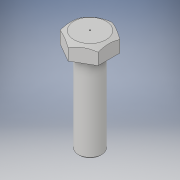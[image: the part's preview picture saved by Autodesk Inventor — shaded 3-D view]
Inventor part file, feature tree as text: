
AUTODESK INVENTOR PART (.ipt)
format: ipt  version: 2019 (Build 230136000, 136)  size: 125,952 bytes
history: native  units: mm
features: sketch x4, extrude x2, chamfer x1, plane x1, revolve x1
ambient origin geometry x8: Origin, YZ Plane, XZ Plane, XY Plane, X Axis, Y Axis, Z Axis, Center Point
bodies: Solid1 (feature_tree)
feature tree (9):
  extrude  "Extrusion1"  Depth=400.0mm
  extrude  "Extrusion2"  Depth=25.0mm TaperAngle=45.0deg
  chamfer  "Chamfer1"  Distance=5.759587mm
  plane  "Work Plane1"
  sketch  "Sketch3"  dims[d10=0.0mm]
  revolve  "Revolution1"  Angle=90.0deg
  sketch  "Sketch1"  dims[d2=265.0mm d3=0.0mm d4=400.0mm]
  sketch  "Sketch2"  dims[d5=1500.0mm d6=0.0mm d7=25.0mm d8=2.0mm d9=45.0deg]
  sketch  "Sketch4"  dims[d11=275.0mm d12=5.759587mm d13=90.0deg]
